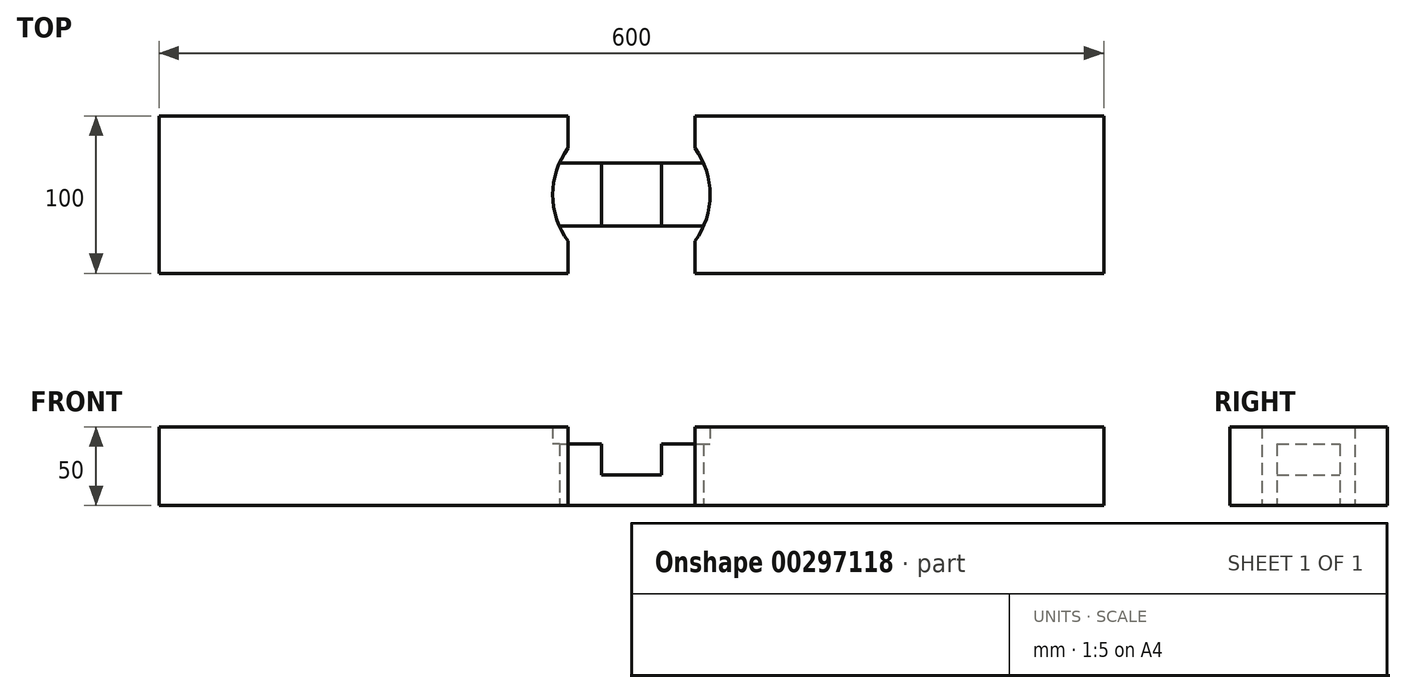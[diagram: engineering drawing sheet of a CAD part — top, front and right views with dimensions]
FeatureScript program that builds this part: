
annotation { "Feature Type Name" : "Feature", "Feature Type Description" : "" }
export const myFeature = defineFeature(function(context is Context, id is Id, definition is map)
    precondition{}
    {
        {
            var Q0;
            Q0=qCreatedBy(makeId("Top.planeOp"),FACE);
            var sketch = newSketch(context, id + "F0", { "sketchPlane" : qUnion([Q0])});
            skLineSegment(sketch, "E0.bottom", {"start": v(150, 50) * mm, "end": v(40.3, 50) * mm});
            skLineSegment(sketch, "E0.top", {"start": v(150, -50) * mm, "end": v(40.3, -50) * mm});
            skLineSegment(sketch, "E0.left", {"start": v(150, 50) * mm, "end": v(150, -50) * mm});
            skPoint(sketch, "E0.middle", {"position": v(0, 0) * mm});
            skLineSegment(sketch, "E1", {"start": v(0, 20) * mm, "end": v(0, -20) * mm});
            skPoint(sketch, "E0.right.start.orphan", {"position": v(-150, 50) * mm});
            skPoint(sketch, "E2.orphan", {"position": v(-150, -50) * mm});
            skLineSegment(sketch, "E3.bottom", {"start": v(0, 20) * mm, "end": v(45.83, 20) * mm});
            skArc(sketch, "E4", {"start": v(40.3, -29.59) * mm, "mid": v(50, 0) * mm, "end": v(40.3, 29.59) * mm});
            skPoint(sketch, "E3.right.start.orphan", {"position": v(50, 20) * mm});
            skLineSegment(sketch, "E5.trimOffspring", {"start": v(0, -20) * mm, "end": v(50, -20) * mm});
            skPoint(sketch, "E3.left.start.orphan", {"position": v(-50, 20) * mm});
            skPoint(sketch, "E3.top.start.orphan", {"position": v(-50, -20) * mm});
            skPoint(sketch, "E6.orphan", {"position": v(0, 50) * mm});
            skPoint(sketch, "E7.orphan", {"position": v(0, -50) * mm});
            skLineSegment(sketch, "E8", {"start": v(40.3, 50) * mm, "end": v(40.3, 29.59) * mm});
            skLineSegment(sketch, "E9.trimOffspring", {"start": v(40.3, -29.59) * mm, "end": v(40.3, -50) * mm});
            skSolve(sketch);
        }
        {
            var Q0;
            {var subQ0=sQuery(id+"F0.wireOp",EDGE,"E1");Q0=makeQuery(id+"F0.imprint","IMPRINT",FACE,{"disambiguationData":[TD([[makeQuery(id+"F0.imprint","IMPRINT",EDGE,{"derivedFrom":subQ0}),1.0]])]});}
            extrude(context, id + "F1", {"entities" : qUnion([Q0]), "depth" : 39 * mm});
        }
        {
            var Q0;
            {var subQ3=sQuery(id+"F0.wireOp",EDGE,"E0.bottom");Q0=makeQuery(id+"F0.imprint","IMPRINT",FACE,{"disambiguationData":[TD([[makeQuery(id+"F0.imprint","IMPRINT",EDGE,{"derivedFrom":subQ3}),1.0]])]});}
            extrude(context, id + "F2", {"entities" : qUnion([Q0]), "operationType" : NewBodyOperationType.ADD, "depth" : 50 * mm});
        }
        {
            var Q0;
            Q0=makeQuery(id+"F2.opExtrude","SWEPT_FACE",FACE,{"disambiguationData":[OSD([sQuery(id+"F0.wireOp",EDGE,"E0.left")])]});
            var sketch = newSketch(context, id + "F3", { "sketchPlane" : qUnion([Q0])});
            skLineSegment(sketch, "E10.bottom", {"start": v(-50, 50) * mm, "end": v(50, 50) * mm});
            skLineSegment(sketch, "E10.top", {"start": v(-50, 0) * mm, "end": v(50, 0) * mm});
            skLineSegment(sketch, "E10.left", {"start": v(-50, 50) * mm, "end": v(-50, 0) * mm});
            skLineSegment(sketch, "E10.right", {"start": v(50, 50) * mm, "end": v(50, 0) * mm});
            skSolve(sketch);
        }
        {
            var Q0;
            Q0 = qSketchRegion(id + "F3", true);
            extrude(context, id + "F4", {"entities" : qUnion([Q0]), "operationType" : NewBodyOperationType.ADD, "depth" : 150 * mm});
        }
        {
            var Q0;
            Q0=makeQuery(id+"F1.opExtrude","SWEPT_BODY",BODY,{"disambiguationData":[OSD([sQuery(id+"F0.wireOp",EDGE,"E1"),sQuery(id+"F0.wireOp",EDGE,"E3.bottom"),sQuery(id+"F0.wireOp",EDGE,"E4"),sQuery(id+"F0.wireOp",EDGE,"E5.trimOffspring")])]});
            var Q1;
            Q1=qCreatedBy(makeId("Right.planeOp"),FACE);
            mirror(context, id + "F5", {"operationType" : NewBodyOperationType.ADD, "entities" : qUnion([Q0]), "mirrorPlane" : qUnion([Q1])});
        }
        {
            var Q0;
            Q0=qCreatedBy(makeId("Front.planeOp"),FACE);
            var sketch = newSketch(context, id + "F6", { "sketchPlane" : qUnion([Q0])});
            skLineSegment(sketch, "E11.bottom", {"start": v(-10, 39) * mm, "end": v(10, 39) * mm});
            skLineSegment(sketch, "E11.left", {"start": v(-10, 39) * mm, "end": v(-10, 19.5) * mm});
            skLineSegment(sketch, "E11.right", {"start": v(10, 39) * mm, "end": v(10, 19.5) * mm});
            skPoint(sketch, "E11.middle", {"position": v(0, 0) * mm});
            skLineSegment(sketch, "E12", {"start": v(-10, 0) * mm, "end": v(10, 0) * mm});
            skPoint(sketch, "E11.top.end.orphan", {"position": v(10, -39) * mm});
            skPoint(sketch, "E11.top.start.orphan", {"position": v(-10, -39) * mm});
            skLineSegment(sketch, "E13", {"start": v(-10, 19.5) * mm, "end": v(10, 19.5) * mm});
            skSolve(sketch);
        }
        {
            var Q0;
            Q0 = qSketchRegion(id + "F6", true);
            extrude(context, id + "F7", {"entities" : qUnion([Q0]), "operationType" : NewBodyOperationType.REMOVE, "endBound" : BoundingType.SYMMETRIC, "depth" : 153.6 * mm});
        }
        {
            var Q0;
            {var subQ0=makeQuery(id+"F1.opExtrude","SWEPT_FACE",FACE,{"disambiguationData":[OSD([sQuery(id+"F0.wireOp",EDGE,"E5.trimOffspring")])]});Q0=makeQuery(id+"F5.boolean.opBoolean","MERGE",FACE,{"derivedFrom":[subQ0,makeQuery(id+"F5.opPattern","COPY",FACE,{"derivedFrom":subQ0,"instanceName":"1"})]});}
            var sketch = newSketch(context, id + "F8", { "sketchPlane" : qUnion([Q0])});
            skLineSegment(sketch, "E14.bottom", {"start": v(-19, 39) * mm, "end": v(19, 39) * mm});
            skLineSegment(sketch, "E14.top", {"start": v(-19, 0) * mm, "end": v(19, 0) * mm});
            skLineSegment(sketch, "E14.left", {"start": v(-19, 39) * mm, "end": v(-19, 0) * mm});
            skLineSegment(sketch, "E14.right", {"start": v(19, 39) * mm, "end": v(19, 0) * mm});
            skPoint(sketch, "E14.middle", {"position": v(0, 19.5) * mm});
            skLineSegment(sketch, "E15", {"start": v(-19, 19.5) * mm, "end": v(19, 19.5) * mm});
            skSolve(sketch);
        }
        {
            var Q0;
            {var subQ1=makeQuery(id+"F7.opExtrude","SWEPT_FACE",FACE,{"disambiguationData":[OSD([sQuery(id+"F6.wireOp",EDGE,"E11.right")])]});var subQ2=sQuery(id+"F0.wireOp",EDGE,"E5.trimOffspring");var subQ3=makeQuery(id+"F1.opExtrude","SWEPT_FACE",FACE,{"disambiguationData":[OSD([subQ2])]});var subQ4=makeQuery(id+"F5.opPattern","COPY",FACE,{"derivedFrom":subQ3,"instanceName":"1"});var subQ5=makeQuery(id+"F7.boolean.opBoolean","INTERSECT",EDGE,{"derivedFrom":[makeQuery(id+"F5.boolean.opBoolean","MERGE",FACE,{"derivedFrom":[subQ3,subQ4]}),subQ1]});Q0=makeQuery(id+"F8.imprint","IMPRINT",FACE,{"disambiguationData":[TD([[makeQuery(id+"F8.imprint","IMPRINT",EDGE,{"derivedFrom":subQ5}),1.0]])]});}
            var Q1;
            {var subQ1=makeQuery(id+"F7.opExtrude","SWEPT_FACE",FACE,{"disambiguationData":[OSD([sQuery(id+"F6.wireOp",EDGE,"E11.left")])]});var subQ2=sQuery(id+"F0.wireOp",EDGE,"E5.trimOffspring");var subQ3=makeQuery(id+"F1.opExtrude","SWEPT_FACE",FACE,{"disambiguationData":[OSD([subQ2])]});var subQ4=makeQuery(id+"F5.opPattern","COPY",FACE,{"derivedFrom":subQ3,"instanceName":"1"});var subQ5=makeQuery(id+"F7.boolean.opBoolean","INTERSECT",EDGE,{"derivedFrom":[makeQuery(id+"F5.boolean.opBoolean","MERGE",FACE,{"derivedFrom":[subQ3,subQ4]}),subQ1]});Q1=makeQuery(id+"F8.imprint","IMPRINT",FACE,{"disambiguationData":[TD([[makeQuery(id+"F8.imprint","IMPRINT",EDGE,{"derivedFrom":subQ5}),-1.0]])]});}
            extrude(context, id + "F9", {"entities" : qUnion([Q0, Q1]), "operationType" : NewBodyOperationType.REMOVE, "endBound" : BoundingType.SYMMETRIC, "depth" : 1234 * mm});
        }
    });
